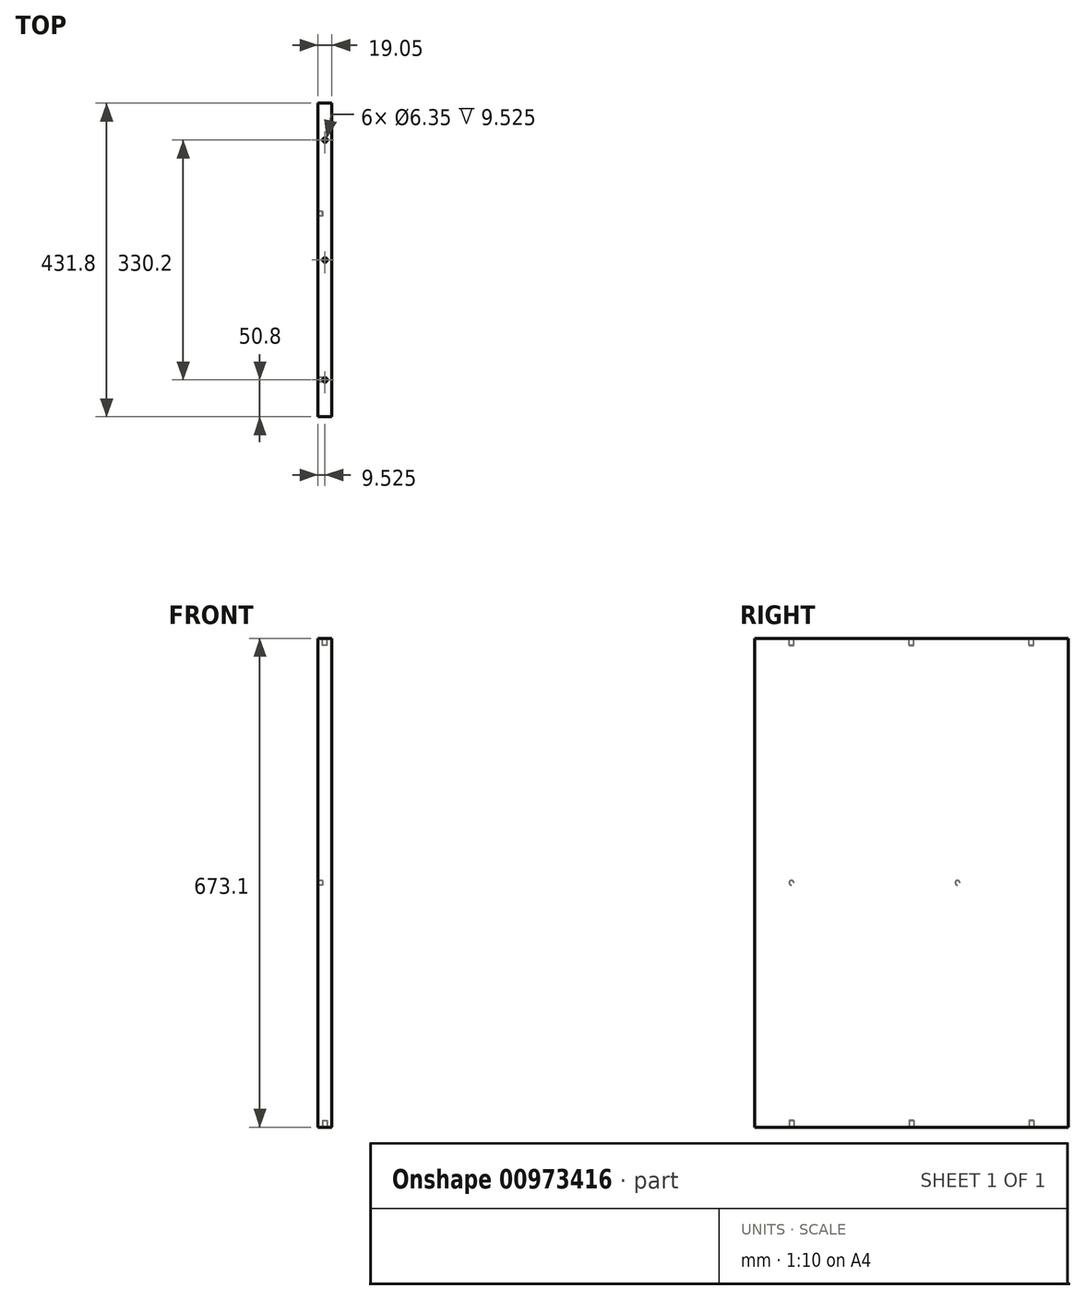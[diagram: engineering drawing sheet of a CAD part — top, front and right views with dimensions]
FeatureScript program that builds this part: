
annotation { "Feature Type Name" : "Feature", "Feature Type Description" : "" }
export const myFeature = defineFeature(function(context is Context, id is Id, definition is map)
    precondition{}
    {
        {
            var Q0;
            Q0=qCreatedBy(makeId("Top.planeOp"),FACE);
            var sketch = newSketch(context, id + "F0", { "sketchPlane" : qUnion([Q0])});
            skLineSegment(sketch, "E0.bottom", {"start": v(0, 0) * mm, "end": v(19.05, 0) * mm});
            skLineSegment(sketch, "E0.top", {"start": v(0, 431.8) * mm, "end": v(19.05, 431.8) * mm});
            skLineSegment(sketch, "E0.left", {"start": v(0, 0) * mm, "end": v(0, 431.8) * mm});
            skLineSegment(sketch, "E0.right", {"start": v(19.05, 0) * mm, "end": v(19.05, 431.8) * mm});
            skSolve(sketch);
        }
        {
            var Q0;
            Q0=makeQuery(id+"F0.imprint","IMPRINT",FACE,{"disambiguationData":[TD([[makeQuery(id+"F0.imprint","IMPRINT",EDGE,{"derivedFrom":sQuery(id+"F0.wireOp",EDGE,"E0.bottom")}),1.0]])]});
            extrude(context, id + "F1", {"entities" : qUnion([Q0]), "depth" : 673.1 * mm, "offsetDistance" : 25.4 * mm});
        }
        {
            var Q0;
            Q0=makeQuery(id+"F1.opExtrude","CAP_FACE",FACE,{"disambiguationData":[OSD([sQuery(id+"F0.wireOp",EDGE,"E0.bottom"),sQuery(id+"F0.wireOp",EDGE,"E0.top"),sQuery(id+"F0.wireOp",EDGE,"E0.left"),sQuery(id+"F0.wireOp",EDGE,"E0.right")])],"isStart":true});
            var sketch = newSketch(context, id + "F2", { "sketchPlane" : qUnion([Q0])});
            skCircle(sketch, "E1", {"center": v(9.53, -50.8) * mm, "radius": 3.18 * mm});
            skCircle(sketch, "E2", {"center": v(9.53, -215.9) * mm, "radius": 3.18 * mm});
            skCircle(sketch, "E3", {"center": v(9.53, -381) * mm, "radius": 3.18 * mm});
            skSolve(sketch);
        }
        {
            var Q0;
            Q0=qSketchRegion(id+"F2",true);
            extrude(context, id + "F3", {"entities" : qUnion([Q0]), "operationType" : NewBodyOperationType.REMOVE, "oppositeDirection" : true, "depth" : 9.52 * mm, "offsetDistance" : 25.4 * mm});
        }
        {
            var Q0;
            Q0=makeQuery(id+"F1.opExtrude","CAP_FACE",FACE,{"disambiguationData":[OSD([sQuery(id+"F0.wireOp",EDGE,"E0.bottom"),sQuery(id+"F0.wireOp",EDGE,"E0.top"),sQuery(id+"F0.wireOp",EDGE,"E0.left"),sQuery(id+"F0.wireOp",EDGE,"E0.right")])],"isStart":false});
            var sketch = newSketch(context, id + "F4", { "sketchPlane" : qUnion([Q0])});
            skCircle(sketch, "E4", {"center": v(9.52, 381) * mm, "radius": 3.18 * mm});
            skCircle(sketch, "E5", {"center": v(9.52, 215.9) * mm, "radius": 3.18 * mm});
            skCircle(sketch, "E6", {"center": v(9.52, 50.8) * mm, "radius": 3.18 * mm});
            skSolve(sketch);
        }
        {
            var Q0;
            Q0=qSketchRegion(id+"F4",true);
            extrude(context, id + "F5", {"entities" : qUnion([Q0]), "operationType" : NewBodyOperationType.REMOVE, "oppositeDirection" : true, "depth" : 9.52 * mm, "offsetDistance" : 25.4 * mm});
        }
        {
            var Q0;
            Q0=makeQuery(id+"F1.opExtrude","SWEPT_FACE",FACE,{"disambiguationData":[OSD([sQuery(id+"F0.wireOp",EDGE,"E0.left")])]});
            var sketch = newSketch(context, id + "F6", { "sketchPlane" : qUnion([Q0])});
            skCircle(sketch, "E7", {"center": v(-279.4, 336.55) * mm, "radius": 3.18 * mm});
            skCircle(sketch, "E8", {"center": v(-50.8, 336.55) * mm, "radius": 3.18 * mm});
            skSolve(sketch);
        }
        {
            var Q0;
            Q0 = qSketchRegion(id + "F6", true);
            extrude(context, id + "F7", {"entities" : qUnion([Q0]), "operationType" : NewBodyOperationType.REMOVE, "oppositeDirection" : true, "depth" : 6.35 * mm, "offsetDistance" : 25.4 * mm});
        }
    });
